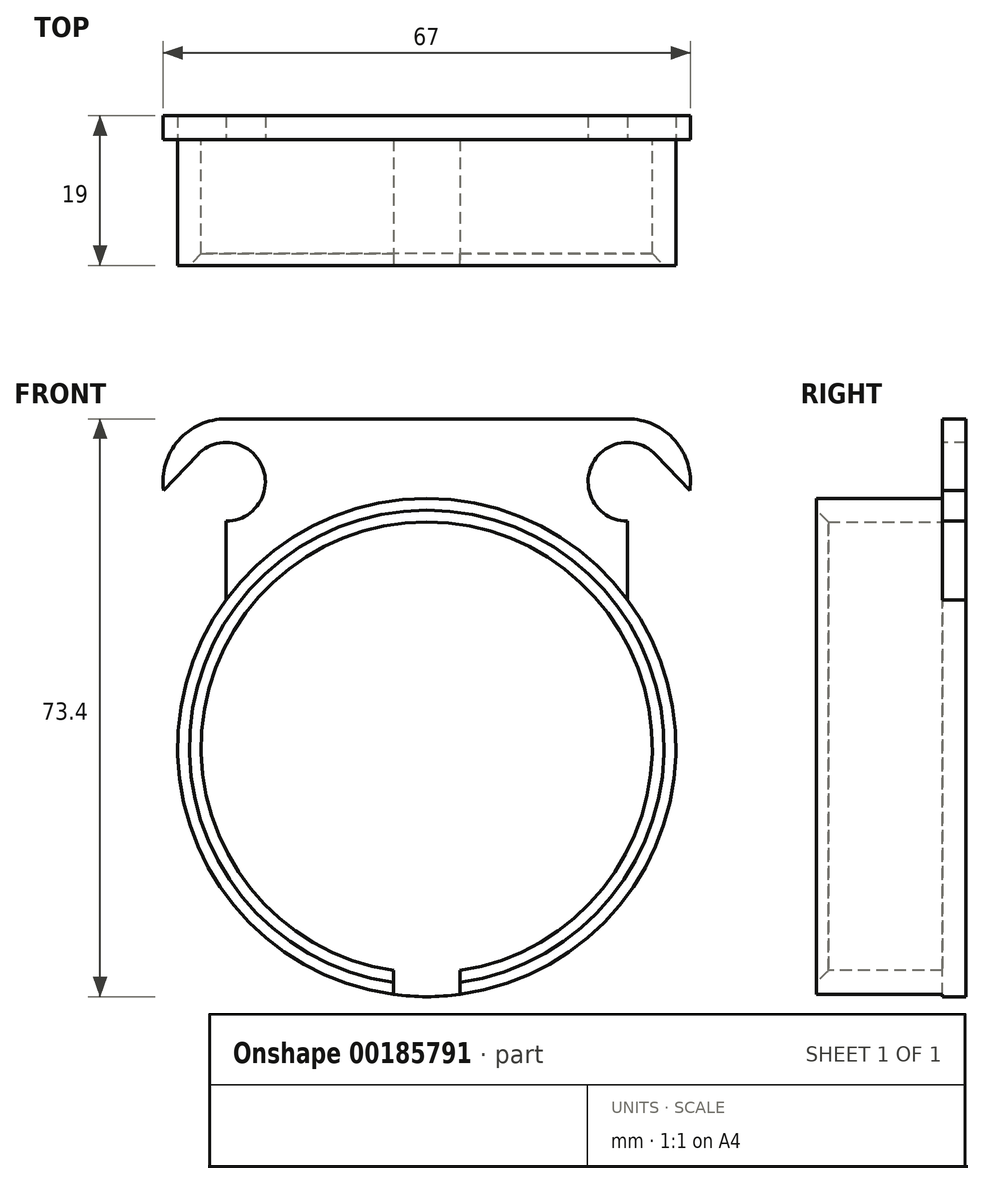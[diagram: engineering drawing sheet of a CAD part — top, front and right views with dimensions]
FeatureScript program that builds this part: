
annotation { "Feature Type Name" : "Feature", "Feature Type Description" : "" }
export const myFeature = defineFeature(function(context is Context, id is Id, definition is map)
    precondition{}
    {
        {
            assignVariable(context, id + "F0", {"name" : "diald", "anyValue" : 26});
        }
        {
            var Q0;
            Q0=qCreatedBy(makeId("Front.planeOp"),FACE);
            var sketch = newSketch(context, id + "F6", { "sketchPlane" : qUnion([Q0])});
            skCircle(sketch, "E0", {"center": v(0, 0) * mm, "radius": 31.65 * mm});
            skLineSegment(sketch, "E1", {"start": v(0, 0) * mm, "end": v(0, 101.72) * mm, "construction": true});
            skPoint(sketch, "E2", {"position": v(0, 31.65) * mm});
            skCircle(sketch, "E3", {"center": v(-25.5, 33.75) * mm, "radius": 5 * mm});
            skCircle(sketch, "E4.0", {"center": v(-25.5, 33.75) * mm, "radius": 8 * mm});
            skLineSegment(sketch, "E5", {"start": v(-17.5, 33.75) * mm, "end": v(-17.5, 26.37) * mm});
            skLineSegment(sketch, "E6", {"start": v(-29.14, 37.18) * mm, "end": v(-33.42, 32.64) * mm});
            skLineSegment(sketch, "E7", {"start": v(-25.5, 25.75) * mm, "end": v(-25.5, 18.75) * mm});
            skLineSegment(sketch, "E8", {"start": v(-25.5, 25.75) * mm, "end": v(-25.5, 28.75) * mm});
            skLineSegment(sketch, "E9.MirrorCS", {"start": v(17.5, 33.75) * mm, "end": v(17.5, 26.37) * mm});
            skLineSegment(sketch, "E10.MirrorCS", {"start": v(25.5, 25.75) * mm, "end": v(25.5, 18.75) * mm});
            skLineSegment(sketch, "E11.MirrorCS", {"start": v(25.5, 25.75) * mm, "end": v(25.5, 28.75) * mm});
            skLineSegment(sketch, "E12.MirrorCS", {"start": v(29.14, 37.18) * mm, "end": v(33.42, 32.64) * mm});
            skCircle(sketch, "E13.MirrorC", {"center": v(25.5, 33.75) * mm, "radius": 8 * mm});
            skCircle(sketch, "E14.MirrorC", {"center": v(25.5, 33.75) * mm, "radius": 5 * mm});
            skCircle(sketch, "E15", {"center": v(0, 0) * mm, "radius": 28.65 * mm});
            skLineSegment(sketch, "E16", {"start": v(25.5, 41.75) * mm, "end": v(-25.5, 41.75) * mm});
            skSolve(sketch);
        }
        {
            var Q0;
            {var subQ4=sQuery(id+"F6.wireOp",EDGE,"E6");Q0=makeQuery(id+"F6.imprint","IMPRINT",FACE,{"disambiguationData":[TD([[makeQuery(id+"F6.imprint","IMPRINT",EDGE,{"derivedFrom":subQ4}),-1.0]])]});}
            var Q1;
            {var subQ0=sQuery(id+"F6.wireOp",EDGE,"E7");Q1=makeQuery(id+"F6.imprint","IMPRINT",FACE,{"disambiguationData":[TD([[makeQuery(id+"F6.imprint","IMPRINT",EDGE,{"derivedFrom":subQ0}),1.0]])]});}
            var Q2;
            {var subQ0=sQuery(id+"F6.wireOp",EDGE,"E5");Q2=makeQuery(id+"F6.imprint","IMPRINT",FACE,{"disambiguationData":[TD([[makeQuery(id+"F6.imprint","IMPRINT",EDGE,{"derivedFrom":subQ0}),-1.0]])]});}
            var Q3;
            {var subQ0=sQuery(id+"F6.wireOp",EDGE,"E9.MirrorCS");Q3=makeQuery(id+"F6.imprint","IMPRINT",FACE,{"disambiguationData":[TD([[makeQuery(id+"F6.imprint","IMPRINT",EDGE,{"derivedFrom":subQ0}),1.0]])]});}
            var Q4;
            {var subQ1=sQuery(id+"F6.wireOp",EDGE,"E11.MirrorCS");Q4=makeQuery(id+"F6.imprint","IMPRINT",FACE,{"disambiguationData":[TD([[makeQuery(id+"F6.imprint","IMPRINT",EDGE,{"derivedFrom":subQ1}),1.0]])]});}
            var Q5;
            {var subQ0=sQuery(id+"F6.wireOp",EDGE,"E10.MirrorCS");Q5=makeQuery(id+"F6.imprint","IMPRINT",FACE,{"disambiguationData":[TD([[makeQuery(id+"F6.imprint","IMPRINT",EDGE,{"derivedFrom":subQ0}),-1.0]])]});}
            var Q6;
            Q6=makeQuery(id+"F6.imprint","IMPRINT",FACE,{"disambiguationData":[TD([[makeQuery(id+"F6.imprint","IMPRINT",EDGE,{"derivedFrom":sQuery(id+"F6.wireOp",EDGE,"E15")}),1.0]])]});
            var Q7;
            Q7=makeQuery(id+"F6.imprint","IMPRINT",FACE,{"disambiguationData":[TD([[makeQuery(id+"F6.imprint","IMPRINT",EDGE,{"derivedFrom":sQuery(id+"F6.wireOp",EDGE,"E15")}),-1.0]])]});
            var Q8;
            {var subQ3=sQuery(id+"F6.wireOp",EDGE,"E5");Q8=makeQuery(id+"F6.imprint","IMPRINT",FACE,{"disambiguationData":[TD([[makeQuery(id+"F6.imprint","IMPRINT",EDGE,{"derivedFrom":subQ3}),1.0]])]});}
            extrude(context, id + "F1", {"entities" : qUnion([Q0, Q1, Q2, Q3, Q4, Q5, Q6, Q7, Q8]), "oppositeDirection" : true, "depth" : 3 * mm});
        }
        {
            var Q0;
            {var subQ0=sQuery(id+"F6.wireOp",EDGE,"E0");var subQ5=makeQuery(id+"F6.imprint","INTERSECT",VERTEX,{"derivedFrom":[subQ0,sQuery(id+"F6.wireOp",EDGE,"E10.MirrorCS")]});Q0=makeQuery(id+"F6.imprint","IMPRINT",FACE,{"disambiguationData":[TD([[makeQuery(id+"F6.imprint","IMPRINT",EDGE,{"disambiguationData":[TD([[subQ5,-1.0]])],"derivedFrom":subQ0}),1.0]])]});}
            extrude(context, id + "F2", {"entities" : qUnion([Q0]), "operationType" : NewBodyOperationType.ADD, "depth" : (getVariable(context, 'diald') - 10) * mm});
        }
        {
            var Q0;
            Q0=makeQuery(id+"F2.opExtrude","CAP_FACE",FACE,{"disambiguationData":[OSD([sQuery(id+"F6.wireOp",EDGE,"E0"),sQuery(id+"F6.wireOp",EDGE,"E15")])],"isStart":false});
            var sketch = newSketch(context, id + "F3", { "sketchPlane" : qUnion([Q0])});
            skLineSegment(sketch, "E17", {"start": v(-4.2, -28.34) * mm, "end": v(-4.2, -31.37) * mm});
            skLineSegment(sketch, "E18", {"start": v(0, 0) * mm, "end": v(0, -15) * mm, "construction": true});
            skLineSegment(sketch, "E19.MirrorCS", {"start": v(4.2, -28.34) * mm, "end": v(4.2, -31.37) * mm});
            skCircle(sketch, "E20.0", {"center": v(0, 0) * mm, "radius": 28.65 * mm, "construction": true});
            skSolve(sketch);
        }
        {
            var Q0;
            {var subQ0=sQuery(id+"F3.wireOp",EDGE,"E17");Q0=makeQuery(id+"F3.imprint","IMPRINT",FACE,{"disambiguationData":[TD([[makeQuery(id+"F3.imprint","IMPRINT",EDGE,{"derivedFrom":subQ0}),1.0]])]});}
            var Q1;
            Q1=makeQuery(id+"F2.boolean.opBoolean","SPLIT",FACE,{"disambiguationData":[TD([makeQuery(id+"F2.opExtrude","SWEPT_FACE",FACE,{"disambiguationData":[OSD([sQuery(id+"F6.wireOp",EDGE,"E15")])]})])],"derivedFrom":makeQuery(id+"F1.opExtrude","CAP_FACE",FACE,{"disambiguationData":[OSD([sQuery(id+"F6.wireOp",EDGE,"E0"),sQuery(id+"F6.wireOp",EDGE,"E3"),sQuery(id+"F6.wireOp",EDGE,"E4.0"),sQuery(id+"F6.wireOp",EDGE,"E5"),sQuery(id+"F6.wireOp",EDGE,"E6"),sQuery(id+"F6.wireOp",EDGE,"E7"),sQuery(id+"F6.wireOp",EDGE,"E8"),sQuery(id+"F6.wireOp",EDGE,"E9.MirrorCS"),sQuery(id+"F6.wireOp",EDGE,"E10.MirrorCS"),sQuery(id+"F6.wireOp",EDGE,"E11.MirrorCS"),sQuery(id+"F6.wireOp",EDGE,"E12.MirrorCS"),sQuery(id+"F6.wireOp",EDGE,"E13.MirrorC"),sQuery(id+"F6.wireOp",EDGE,"E14.MirrorC")])],"isStart":true})});
            extrude(context, id + "F4", {"entities" : qUnion([Q0]), "operationType" : NewBodyOperationType.REMOVE, "endBound" : BoundingType.UP_TO_SURFACE, "oppositeDirection" : true, "endBoundEntityFace" : qUnion([Q1]), "depth" : (((getVariable(context, 'diald') / 2) + 4) + .5) * mm});
        }
        {
            var Q0;
            Q0=makeQuery(id+"F2.opExtrude","CAP_EDGE",EDGE,{"disambiguationData":[OSD([sQuery(id+"F6.wireOp",EDGE,"E15")])],"isStart":false});
            chamfer(context, id + "F5", {"entities" : qUnion([Q0]), "width" : 1.5 * mm, "tangentPropagation" : true});
        }
    });
